# Revit family: Buderus-Boiler-GE515_Floor_Standing_High_Efficiency_Boiler-141
name_source: partatom
category: Mechanical Equipment
revit_build: Autodesk Revit 2014 (Build: 20130308_1515(x64)
units: mm (PartAtom-declared; Revit-internal decimal feet)

## types (2) — shared parameters
6 Monthly = service when oil fired
Access Clearance Bottom = 0
Access Clearance Front = 2200 (1000 with shorter cleaning rods)
Access Clearance Left = 400 (depending on door handing)
Access Clearance Rear = 900
Access Clearance Right = 680
Access Clearance Top = 0
Air Exhaust Connection Size (Inch) = 10
Annually = Annual service
Assembly Code = D3020100
AssetType = Fixed
BMS Links = Yes
Bespoke Timeframe = No
Building Regulations Seasonal Efficiency = 86.5
Burner B = 229 mm
Burner C = 152 mm
Burner Configuration = Separate
Burner H = 483 mm
Burner L = 584 mm
Burner W = 483 mm
CE Approval = CE0461AR6154
ClassificationName = Uniclass2015
ClassificationValue = Pr_60_60_08_24
Color = RAL 5015
Colour = Blue RAL classic 5015
Condensate Drain Type = Unset
Configuration = Single Boiler
Constituents = Cast iron, steel, polymers
Control Options = Unset
Control Type = External
Daily = No
Description = The Buderus GE series includes a robust range of Ecostream boilers constructed from special Buderus GL 180 M grey cast iron which makes them extremely resistant to corrosion and high temperatures.
DocumentationInstallationGuide = https://specifi.bimstore.co.uk
DocumentationLiterature = https://specifi.bimstore.co.uk
DocumentationMaintenance = https://specifi.bimstore.co.uk
DocumentationTechnical = https://specifi.bimstore.co.uk
Drain Connection Size = R 3/4"
Drain Connection Type = Threaded
DurationUnit = Years
ErP Energy Label = N
Expected Life = 20 - 30
External Material = Steel
Features = High Efficiency Cast Iron Boiler
Finish = Paint
Flow and Return Connection Size = DN 100
Flow and Return Connection Type = Flanged
Flue Connection Size = 250
Flue or Air Intake Classification = B23
Frequency = 50
Fuel Connection Size = R 2"
Fuel Connection Type = Unset
Full Load Current = 1.7 (dependent on burner used)
Fuse Rating = 10
Gas Consumption rate = 50.6
Heat Exchanger Material = Cast Iron
IP Rating = dependent on burner used
Interlocks = Yes
Keynote = T24/310
LG = 1581 mm
Maintenance Required 0-300hrs = No
Maintenance Required 1001-2000hrs = No
Maintenance Required 2001-4000hrs = No
Maintenance Required 301-600hrs = No
Maintenance Required 4001-8000hrs = No
Maintenance Required 601-1000hrs = No
Maintenance Required 8001-12000hrs = No
Manufacturer = Bosch Thermotechnology
Material = Cast Iron
Maximum Gas Inlet Pressure = 25
Maximum Oil Inlet Pressure = 400
Maximum Operating Pressure = 6
Maximum Power Consumption = dependent on burner used
Minimum Gas Inlet Pressure = 16.1 (dependent on gas train used)
Minimum Oil Inlet Pressure = -0.40 (for twin pipe circuits)
Minimum Operating Pressure = 0.8
Minimum Power Consumption = dependent on burner used
Model = GE515 Floor Standing High Efficiency Boiler
ModelNumber = GE515 Floor Standing High Efficiency Boiler
Monthly = No
Mounting = Floor Standing
NBSObjectName = Dual fuel fired cast iron boilers
NBSReference = 90-40-05/310
NOx Emissions = 120 - gas   140 - Oil
Nominal Gas Inlet Pressure = 20
Nominal Oil Inlet Pressure = 50
O&M Manual = https://specifi.bimstore.co.uk
Oil Consumption rate = 41.3
Overall Height = 1556
Overall Width = 980
Primary Fuel = Gas - NG
Product Literature = http://www.buderus.co.uk
Product Range = GE515
ProductionYear = 2015
Quaterly = No
Rated Criteria = 80/60
Rated Efficiency at Part Load = 96.7
ReferencedStandard = BS EN
Return Water Connection Size (Inch) = 4
Safety Valve Connection Size = R11/2" (when using optional safety manifold)
Safety Valve Connection Type = Flanged
Secondary Fuel = Oil - 35/sec
Shape = Rectangular (Horizontal)
Sound Pressure Level = 72 (dependent on burner)
Standard Relief Valve Rating (PSIG) = 50
Starting Current = 3 (dependent on burner used)
Supply Phase = 1ph - controls 3ph - burner
Supply Water Connection Size (Inch) = 4
Total Width = 978 mm
Turndown Ratio = dependent on burner used
Type = Space Heating
URL = http://www.buderus.co.uk
Voltage = 230 - controls 400 - burner
Warranty ID = Serial number and end user registration
WarrantyDurationUnit = Years
Weekly = System pressure check
Width 1 = 789 mm
_current revision = 1
_distributed by = www.bimstore.co.uk
zero-valued in all types: _BIMspec_GUID

## per-type parameters (varying)
| type | ExpectedLife | Gross Weight | LK | Overall Length | Rated Efficiency at Full Load | Rated Output | Shipping Weight | Type Comments | TypeName | Water Content |
| 455kW | 0 | 2302 | 2267 mm | 2260 | 93.0 | 401 - 455 | 1900 | G515 - 455kW | G515 - 455kW | 402 |
| 510kW | 25 | 2498 | 2438 mm | 2430 | 93.1 | 456 - 510 | 2060 | G515 - 510kW | G515 - 510kW | 438 |

note: column(s) folded — value = type name in every type: Product Model Number

## geometry (parser evidence)
native form markers: Sweep x1
no freeform markers — native parametric forms only
